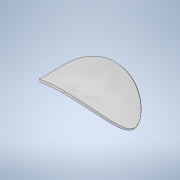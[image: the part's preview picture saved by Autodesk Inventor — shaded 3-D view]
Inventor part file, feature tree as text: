
AUTODESK INVENTOR PART (.ipt)
format: ipt  version: 2022 (Build 260153070, 153G)  size: 489,472 bytes
history: native  units: mm
features: other x6, sketch x4, plane x2, extrude x2, thicken_offset x1, surface_op x1
ambient origin geometry x8: Origin, YZ Plane, XZ Plane, XY Plane, X Axis, Y Axis, Z Axis, Center Point
bodies: Body1 (feature_tree), Body2 (feature_tree), Body3 (feature_tree), Body4 (feature_tree)
feature tree (16):
  other  "Work Axis1"
  plane  "Work Plane1"
  sketch  "Sketch3"  dims[d10=1.5875mm d11=0.1mm]
  plane  "Work Plane3"
  thicken_offset  "Thicken2"
  other  "Work Axis3"
  other  "Work Point1"
  sketch  "Sketch1"  dims[d0=45.72mm d1=0.0mm d2=10.0mm d3=0.0mm]
  other  "Srf1"
  sketch  "Sketch2"  dims[d8=5.0mm d9=0.0mm]
  other  "Srf2"
  sketch  "Sketch4"  dims[d13=19.05mm d14=75.692mm]
  other  "Srf4"
  extrude  "ExtrusionSrf1"  Depth=10.0mm TaperAngle=0.0deg
  extrude  "ExtrusionSrf2"  TaperAngle=0.0deg  [1 undecoded]
  surface_op  "Boundary Patch2"
note: 1 required parameter value undecoded (feature->parameter linkage not recoverable at this tier; creation-order binding heuristic only, values carry confidence <= 0.55)
